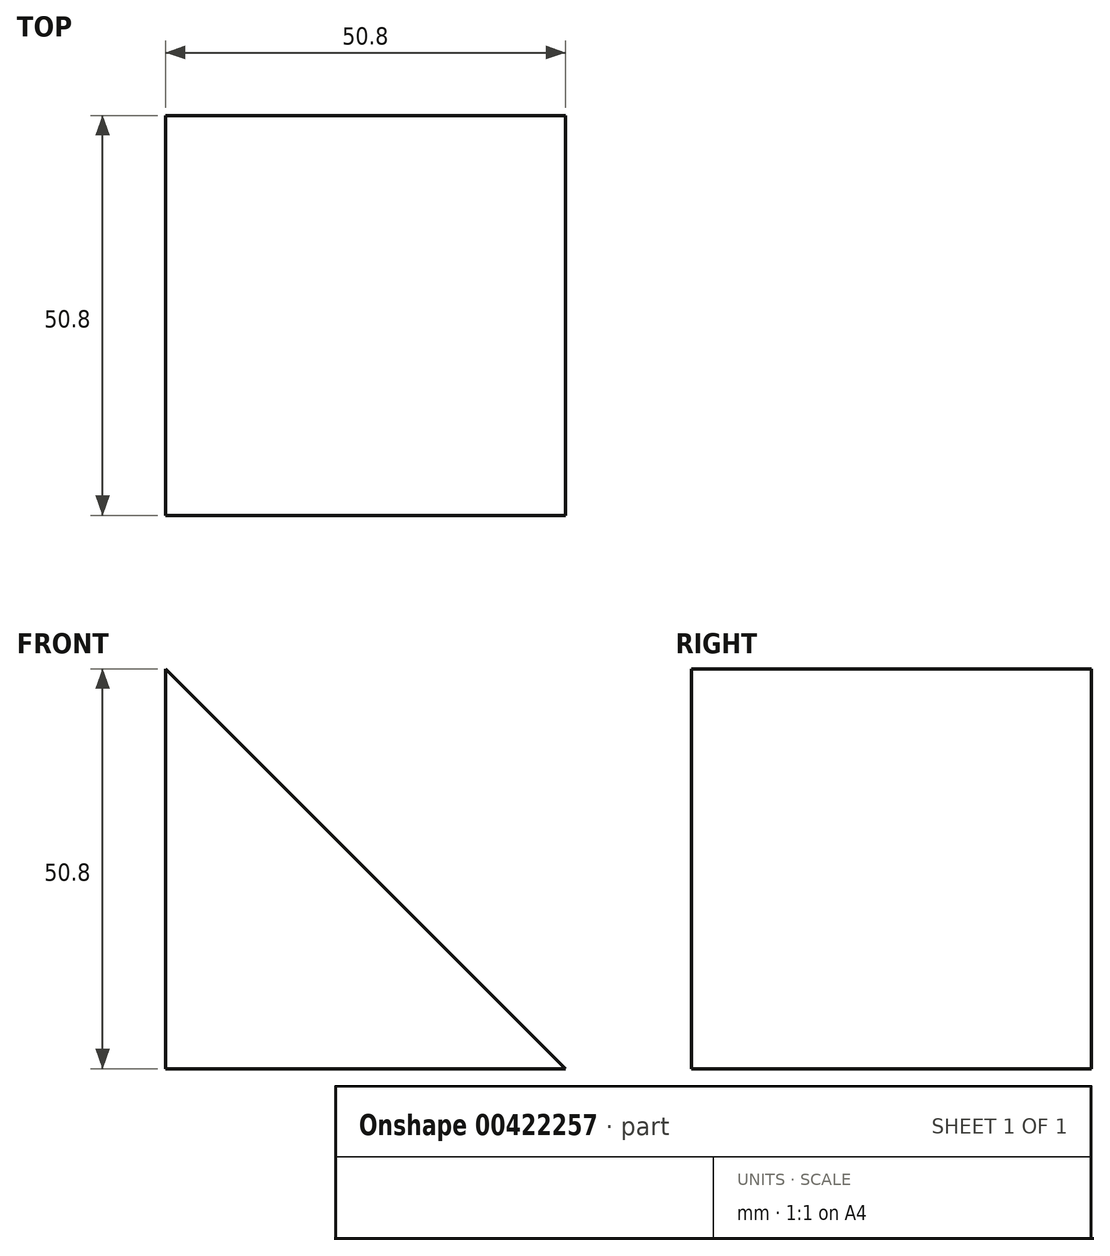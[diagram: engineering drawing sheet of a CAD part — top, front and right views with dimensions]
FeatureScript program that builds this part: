
annotation { "Feature Type Name" : "Feature", "Feature Type Description" : "" }
export const myFeature = defineFeature(function(context is Context, id is Id, definition is map)
    precondition{}
    {
        {
            var Q0;
            Q0=qCreatedBy(makeId("Front.planeOp"),FACE);
            var sketch = newSketch(context, id + "F0", { "sketchPlane" : qUnion([Q0])});
            skLineSegment(sketch, "E0", {"start": v(-50.8, 50.8) * mm, "end": v(-50.8, 0) * mm});
            skLineSegment(sketch, "E1", {"start": v(-50.8, 0) * mm, "end": v(0, 0) * mm});
            skLineSegment(sketch, "E2", {"start": v(-50.8, 50.8) * mm, "end": v(0, 0) * mm});
            skSolve(sketch);
        }
        {
            var Q0;
            Q0 = qSketchRegion(id + "F0", true);
            extrude(context, id + "F1", {"entities" : qUnion([Q0]), "depth" : 50.8 * mm});
        }
    });
